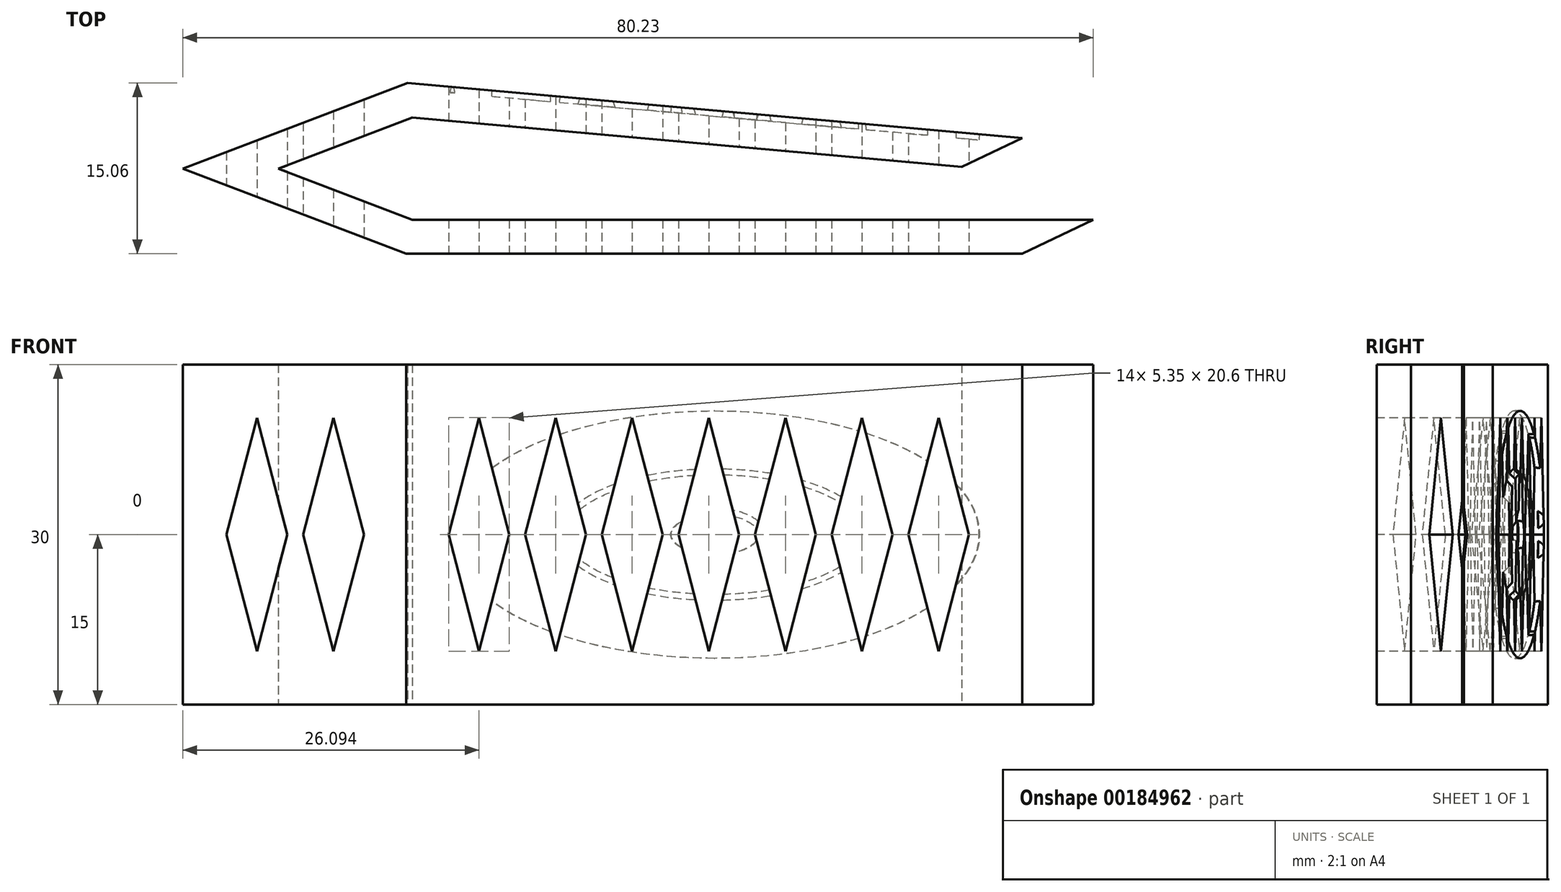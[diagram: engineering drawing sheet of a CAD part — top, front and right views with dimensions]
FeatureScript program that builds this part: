
annotation { "Feature Type Name" : "Feature", "Feature Type Description" : "" }
export const myFeature = defineFeature(function(context is Context, id is Id, definition is map)
    precondition{}
    {
        {
            var Q0;
            Q0=qCreatedBy(makeId("Top.planeOp"),FACE);
            var sketch = newSketch(context, id + "F0", { "sketchPlane" : qUnion([Q0])});
            skLineSegment(sketch, "E0", {"start": v(30.5, 0) * mm, "end": v(-29.5, 0) * mm});
            skLineSegment(sketch, "E1", {"start": v(-29.5, 9) * mm, "end": v(18.93, 4.67) * mm});
            skLineSegment(sketch, "E2", {"start": v(18.93, 4.67) * mm, "end": v(24.23, 7.2) * mm});
            skLineSegment(sketch, "E3", {"start": v(24.23, -3) * mm, "end": v(30.5, 0) * mm});
            skLineSegment(sketch, "E4.0", {"start": v(-29.92, 12.06) * mm, "end": v(24.23, 7.2) * mm});
            skLineSegment(sketch, "E5.0", {"start": v(24.23, -3) * mm, "end": v(-30.05, -3) * mm});
            skLineSegment(sketch, "E6", {"start": v(-29.5, 9) * mm, "end": v(-29.5, 0) * mm, "construction": true});
            skLineSegment(sketch, "E7", {"start": v(-29.5, 4.5) * mm, "end": v(-112.6, 4.5) * mm, "construction": true});
            skLineSegment(sketch, "E8", {"start": v(-29.5, 9) * mm, "end": v(-41.3, 4.5) * mm});
            skLineSegment(sketch, "E9", {"start": v(-41.3, 4.5) * mm, "end": v(-29.5, 0) * mm});
            skLineSegment(sketch, "E10", {"start": v(-29.92, 12.06) * mm, "end": v(-49.73, 4.5) * mm});
            skLineSegment(sketch, "E11", {"start": v(-49.73, 4.5) * mm, "end": v(-30.05, -3) * mm});
            skPoint(sketch, "E12.orphan", {"position": v(30.5, -3) * mm});
            skLineSegment(sketch, "E13", {"start": v(-38.13, 8.93) * mm, "end": v(-37.06, 6.12) * mm, "construction": true});
            skLineSegment(sketch, "E14", {"start": v(-34.51, 1.91) * mm, "end": v(-35.58, -0.9) * mm, "construction": true});
            skLineSegment(sketch, "E15", {"start": v(-29.92, 12.06) * mm, "end": v(-30.05, -3) * mm, "construction": true});
            skLineSegment(sketch, "E16", {"start": v(18.93, 4.67) * mm, "end": v(18.93, 0) * mm, "construction": true});
            skSolve(sketch);
        }
        {
            var Q0;
            Q0=makeQuery(id+"F0.imprint","IMPRINT",FACE,{"disambiguationData":[TD([[makeQuery(id+"F0.imprint","IMPRINT",EDGE,{"derivedFrom":sQuery(id+"F0.wireOp",EDGE,"E0")}),1.0]])]});
            extrude(context, id + "F1", {"entities" : qUnion([Q0]), "endBound" : BoundingType.SYMMETRIC, "depth" : 30 * mm});
        }
        {
            var Q0;
            Q0=makeQuery(id+"F1.opExtrude","SWEPT_FACE",FACE,{"disambiguationData":[OSD([sQuery(id+"F0.wireOp",EDGE,"E4.0")])]});
            cPlane(context, id + "F2", {"entities" : qUnion([Q0]), "cplaneType" : CPlaneType.OFFSET, "offset" : 0 * mm, "width" : 150 * mm, "height" : 150 * mm});
        }
        {
            var Q0;
            Q0=qCreatedBy(id+"F2.planeOp",FACE);
            var sketch = newSketch(context, id + "F3", { "sketchPlane" : qUnion([Q0])});
            skPoint(sketch, "E17.middle", {"position": v(3.69, 0) * mm});
            skPoint(sketch, "E18.orphan", {"position": v(19.84, -6.45) * mm});
            skPoint(sketch, "E19.orphan", {"position": v(27.88, -12.16) * mm});
            skPoint(sketch, "E20.orphan", {"position": v(-20.5, 12.16) * mm});
            skPoint(sketch, "E21.orphan", {"position": v(-12.47, 6.45) * mm});
            skPoint(sketch, "E22.orphan", {"position": v(-3.06, 2.36) * mm});
            skPoint(sketch, "E23.orphan", {"position": v(10.44, -2.36) * mm});
            skPoint(sketch, "E24.start.orphan", {"position": v(3.69, -15.05) * mm});
            skPoint(sketch, "E25.orphan", {"position": v(3.69, 15) * mm});
            skLineSegment(sketch, "E26.trimOffspring", {"start": v(-3.06, 0) * mm, "end": v(-3.2, 0) * mm});
            skLineSegment(sketch, "E27.trimOffspring", {"start": v(10.73, 0) * mm, "end": v(10.44, 0) * mm});
            skPoint(sketch, "E28.start.orphan", {"position": v(30.85, 0) * mm});
            skPoint(sketch, "E29.trimOffspring.end.orphan", {"position": v(-23.48, 0) * mm});
            skPoint(sketch, "E30.orphan", {"position": v(-23.48, -15.05) * mm});
            skPoint(sketch, "E31.orphan", {"position": v(30.85, -15.05) * mm});
            skPoint(sketch, "E32.orphan", {"position": v(30.85, 15) * mm});
            skPoint(sketch, "E33.top.end.orphan", {"position": v(-23.48, 15) * mm});
            skEllipse(sketch, "E34", {"center": v(3.69, 0) * mm, "majorRadius": 23.4 * mm, "minorRadius": 10.9 * mm, "majorAxis": v(1, 0)});
            skEllipse(sketch, "E35", {"center": v(3.69, 0) * mm, "majorRadius": 13.72 * mm, "minorRadius": 5.78 * mm, "majorAxis": v(1, 0)});
            skEllipse(sketch, "E36", {"center": v(3.69, 0) * mm, "majorRadius": 3.87 * mm, "minorRadius": 1.8 * mm, "majorAxis": v(1, 0)});
            skSolve(sketch);
        }
        {
            var Q0;
            Q0=qCreatedBy(makeId("Front.planeOp"),FACE);
            var sketch = newSketch(context, id + "F4", { "sketchPlane" : qUnion([Q0])});
            skLineSegment(sketch, "E37", {"start": v(-29.93, 0) * mm, "end": v(-49.72, 0) * mm});
            skPoint(sketch, "E38.middle", {"position": v(-39.83, 0) * mm});
            skPoint(sketch, "E39.orphan", {"position": v(-33.77, 10.3) * mm});
            skPoint(sketch, "E40.orphan", {"position": v(-45.88, -10.3) * mm});
            skPoint(sketch, "E41.start.orphan", {"position": v(-39.83, 15.06) * mm});
            skPoint(sketch, "E42.orphan", {"position": v(-29.93, 15.06) * mm});
            skPoint(sketch, "E43.trimOffspring.end.orphan", {"position": v(-39.83, -14.93) * mm});
            skPoint(sketch, "E44.orphan", {"position": v(-29.93, -14.93) * mm});
            skPoint(sketch, "E45.orphan", {"position": v(-49.72, -14.93) * mm});
            skPoint(sketch, "E46.bottom.end.orphan", {"position": v(-49.72, 15.06) * mm});
            skPoint(sketch, "E47.orphan", {"position": v(-45.88, 10.3) * mm});
            skPoint(sketch, "E48.orphan", {"position": v(-33.77, -10.3) * mm});
            skLineSegment(sketch, "E49", {"start": v(-43.2, 10.3) * mm, "end": v(-45.88, 0) * mm});
            skLineSegment(sketch, "E50", {"start": v(-43.2, -10.3) * mm, "end": v(-45.88, 0) * mm});
            skLineSegment(sketch, "E51", {"start": v(-43.2, -10.3) * mm, "end": v(-40.53, 0) * mm});
            skLineSegment(sketch, "E52", {"start": v(-40.53, 0) * mm, "end": v(-43.2, 10.3) * mm});
            skLineSegment(sketch, "E53", {"start": v(-36.45, -10.3) * mm, "end": v(-33.77, 0) * mm});
            skLineSegment(sketch, "E54", {"start": v(-36.45, 10.3) * mm, "end": v(-39.13, 0) * mm});
            skLineSegment(sketch, "E55", {"start": v(-39.13, 0) * mm, "end": v(-36.45, -10.3) * mm});
            skLineSegment(sketch, "E56", {"start": v(-33.77, 0) * mm, "end": v(-36.45, 10.3) * mm});
            skLineSegment(sketch, "E57", {"start": v(-39.13, 0) * mm, "end": v(-33.77, 0) * mm, "construction": true});
            skLineSegment(sketch, "E58", {"start": v(-36.45, 10.3) * mm, "end": v(-36.45, -10.3) * mm, "construction": true});
            skLineSegment(sketch, "E59", {"start": v(-24.21, 10.3) * mm, "end": v(20.79, 10.3) * mm, "construction": true});
            skLineSegment(sketch, "E60", {"start": v(-24.21, -10.3) * mm, "end": v(16.14, -10.3) * mm, "construction": true});
            skLineSegment(sketch, "E61", {"start": v(0, 0) * mm, "end": v(-0.7, 0) * mm, "construction": true});
            skPoint(sketch, "E62", {"position": v(-0.7, 0) * mm});
            skLineSegment(sketch, "E63", {"start": v(-0.7, 0) * mm, "end": v(-6.05, 0) * mm, "construction": true});
            skLineSegment(sketch, "E64", {"start": v(-6.05, 0) * mm, "end": v(-7.45, 0) * mm, "construction": true});
            skLineSegment(sketch, "E65", {"start": v(-7.45, 0) * mm, "end": v(-12.8, 0) * mm, "construction": true});
            skLineSegment(sketch, "E66", {"start": v(-12.8, 0) * mm, "end": v(-14.2, 0) * mm, "construction": true});
            skLineSegment(sketch, "E67", {"start": v(-14.2, 0) * mm, "end": v(-19.56, 0) * mm, "construction": true});
            skLineSegment(sketch, "E68", {"start": v(-19.56, 0) * mm, "end": v(-20.96, 0) * mm, "construction": true});
            skLineSegment(sketch, "E69", {"start": v(-20.96, 0) * mm, "end": v(-26.31, 0) * mm, "construction": true});
            skLineSegment(sketch, "E70", {"start": v(0, 0) * mm, "end": v(0.7, 0) * mm, "construction": true});
            skLineSegment(sketch, "E71", {"start": v(0.7, 0) * mm, "end": v(6.05, 0) * mm, "construction": true});
            skLineSegment(sketch, "E72", {"start": v(6.05, 0) * mm, "end": v(7.45, 0) * mm, "construction": true});
            skLineSegment(sketch, "E73", {"start": v(7.45, 0) * mm, "end": v(12.8, 0) * mm, "construction": true});
            skLineSegment(sketch, "E74", {"start": v(12.8, 0) * mm, "end": v(14.2, 0) * mm, "construction": true});
            skLineSegment(sketch, "E75", {"start": v(14.2, 0) * mm, "end": v(19.56, 0) * mm, "construction": true});
            skLineSegment(sketch, "E76", {"start": v(-16.88, 0) * mm, "end": v(-16.88, 13.87) * mm, "construction": true});
            skLineSegment(sketch, "E77", {"start": v(-23.64, 0) * mm, "end": v(-23.64, 13.87) * mm, "construction": true});
            skLineSegment(sketch, "E78", {"start": v(-10.13, 0) * mm, "end": v(-10.13, 13.87) * mm, "construction": true});
            skLineSegment(sketch, "E79", {"start": v(-3.38, 0) * mm, "end": v(-3.38, 12.97) * mm, "construction": true});
            skLineSegment(sketch, "E80", {"start": v(3.38, 0) * mm, "end": v(3.38, 12.97) * mm, "construction": true});
            skLineSegment(sketch, "E81", {"start": v(10.13, 0) * mm, "end": v(10.13, 12.97) * mm, "construction": true});
            skLineSegment(sketch, "E82", {"start": v(16.88, 0) * mm, "end": v(16.88, 13.87) * mm, "construction": true});
            skLineSegment(sketch, "E83", {"start": v(-23.64, 0) * mm, "end": v(-23.64, -18.45) * mm, "construction": true});
            skLineSegment(sketch, "E84", {"start": v(-16.88, -17.49) * mm, "end": v(-16.88, 0) * mm, "construction": true});
            skLineSegment(sketch, "E85", {"start": v(-10.13, 0) * mm, "end": v(-10.13, -16.11) * mm, "construction": true});
            skLineSegment(sketch, "E86", {"start": v(-3.38, 0) * mm, "end": v(-3.38, -17.14) * mm, "construction": true});
            skLineSegment(sketch, "E87", {"start": v(3.38, -17.35) * mm, "end": v(3.38, 0) * mm, "construction": true});
            skLineSegment(sketch, "E88", {"start": v(10.13, 0) * mm, "end": v(10.13, -19.76) * mm, "construction": true});
            skLineSegment(sketch, "E89", {"start": v(16.88, -18.52) * mm, "end": v(16.88, 0) * mm, "construction": true});
            skLineSegment(sketch, "E90", {"start": v(-26.31, 0) * mm, "end": v(-23.64, 10.3) * mm});
            skLineSegment(sketch, "E91", {"start": v(-23.64, 10.3) * mm, "end": v(-20.96, 0) * mm});
            skLineSegment(sketch, "E92", {"start": v(-26.31, 0) * mm, "end": v(-23.64, -10.3) * mm});
            skLineSegment(sketch, "E93", {"start": v(-23.64, -10.3) * mm, "end": v(-20.96, 0) * mm});
            skLineSegment(sketch, "E94", {"start": v(-19.56, 0) * mm, "end": v(-16.88, 10.3) * mm});
            skLineSegment(sketch, "E95", {"start": v(-16.88, 10.3) * mm, "end": v(-14.2, 0) * mm});
            skLineSegment(sketch, "E96", {"start": v(-16.88, -10.3) * mm, "end": v(-14.2, 0) * mm});
            skLineSegment(sketch, "E97", {"start": v(-16.88, -10.3) * mm, "end": v(-19.56, 0) * mm});
            skLineSegment(sketch, "E98", {"start": v(-12.8, 0) * mm, "end": v(-10.13, 10.3) * mm});
            skLineSegment(sketch, "E99", {"start": v(-10.13, 10.3) * mm, "end": v(-7.45, 0) * mm});
            skLineSegment(sketch, "E100", {"start": v(-12.8, 0) * mm, "end": v(-10.13, -10.3) * mm});
            skLineSegment(sketch, "E101", {"start": v(-10.13, -10.3) * mm, "end": v(-7.45, 0) * mm});
            skLineSegment(sketch, "E102", {"start": v(-3.38, 10.3) * mm, "end": v(-6.05, 0) * mm});
            skLineSegment(sketch, "E103", {"start": v(-3.38, -10.3) * mm, "end": v(-0.7, 0) * mm});
            skLineSegment(sketch, "E104", {"start": v(-3.38, 10.3) * mm, "end": v(-0.7, 0) * mm});
            skLineSegment(sketch, "E105", {"start": v(-3.38, -10.3) * mm, "end": v(-6.05, 0) * mm});
            skLineSegment(sketch, "E106", {"start": v(3.38, 10.3) * mm, "end": v(0.7, 0) * mm});
            skLineSegment(sketch, "E107", {"start": v(3.38, -10.3) * mm, "end": v(6.05, 0) * mm});
            skLineSegment(sketch, "E108", {"start": v(3.38, 10.3) * mm, "end": v(6.05, 0) * mm});
            skLineSegment(sketch, "E109", {"start": v(0.7, 0) * mm, "end": v(3.38, -10.3) * mm});
            skLineSegment(sketch, "E110", {"start": v(10.13, -10.3) * mm, "end": v(12.8, 0) * mm});
            skLineSegment(sketch, "E111", {"start": v(10.13, 10.3) * mm, "end": v(12.8, 0) * mm});
            skLineSegment(sketch, "E112", {"start": v(14.2, 0) * mm, "end": v(16.88, 10.3) * mm});
            skLineSegment(sketch, "E113", {"start": v(16.88, 10.3) * mm, "end": v(19.56, 0) * mm});
            skLineSegment(sketch, "E114", {"start": v(16.88, -10.3) * mm, "end": v(14.2, 0) * mm});
            skLineSegment(sketch, "E115", {"start": v(19.56, 0) * mm, "end": v(16.88, -10.3) * mm});
            skLineSegment(sketch, "E116", {"start": v(10.13, -10.3) * mm, "end": v(7.45, 0) * mm});
            skLineSegment(sketch, "E117", {"start": v(10.13, 10.3) * mm, "end": v(7.45, 0) * mm});
            skSolve(sketch);
        }
        {
            var Q0;
            Q0 = qSketchRegion(id + "F4", true);
            extrude(context, id + "F5", {"entities" : qUnion([Q0]), "operationType" : NewBodyOperationType.REMOVE, "endBound" : BoundingType.SYMMETRIC, "oppositeDirection" : true, "depth" : 25 * mm});
        }
        {
            var Q0;
            Q0=makeQuery(id+"F3.imprint","IMPRINT",FACE,{"disambiguationData":[TD([[makeQuery(id+"F3.imprint","IMPRINT",EDGE,{"derivedFrom":sQuery(id+"F3.wireOp",EDGE,"E34")}),1.0]])]});
            extrude(context, id + "F6", {"entities" : qUnion([Q0]), "operationType" : NewBodyOperationType.REMOVE, "oppositeDirection" : true, "depth" : .5 * mm});
        }
        {
            var Q0;
            Q0=makeQuery(id+"F3.imprint","IMPRINT",FACE,{"disambiguationData":[TD([[makeQuery(id+"F3.imprint","IMPRINT",EDGE,{"derivedFrom":sQuery(id+"F3.wireOp",EDGE,"E36")}),1.0]])]});
            extrude(context, id + "F7", {"entities" : qUnion([Q0]), "operationType" : NewBodyOperationType.REMOVE, "oppositeDirection" : true, "depth" : .5 * mm});
        }
        {
            var Q0;
            {var subQ1=sQuery(id+"F3.wireOp",EDGE,"E34");var subQ2=makeQuery(id+"F1.opExtrude","SWEPT_FACE",FACE,{"disambiguationData":[OSD([sQuery(id+"F0.wireOp",EDGE,"E1")])]});Q0=makeQuery(id+"F6.boolean.opBoolean","COPY",EDGE,{"disambiguationData":[TD([makeQuery(id+"F5.boolean.opBoolean","COPY",FACE,{"disambiguationData":[TD([subQ2])],"derivedFrom":makeQuery(id+"F5.opExtrude","SWEPT_FACE",FACE,{"disambiguationData":[OSD([sQuery(id+"F4.wireOp",EDGE,"E95")])]})})])],"derivedFrom":makeQuery(id+"F6.opExtrude","CAP_EDGE",EDGE,{"disambiguationData":[OSD([subQ1])],"isStart":true})});}
            var Q1;
            {var subQ1=sQuery(id+"F3.wireOp",EDGE,"E34");var subQ2=makeQuery(id+"F1.opExtrude","SWEPT_FACE",FACE,{"disambiguationData":[OSD([sQuery(id+"F0.wireOp",EDGE,"E1")])]});Q1=makeQuery(id+"F6.boolean.opBoolean","COPY",EDGE,{"disambiguationData":[TD([makeQuery(id+"F5.boolean.opBoolean","COPY",FACE,{"disambiguationData":[TD([subQ2])],"derivedFrom":makeQuery(id+"F5.opExtrude","SWEPT_FACE",FACE,{"disambiguationData":[OSD([sQuery(id+"F4.wireOp",EDGE,"E111")])]})})])],"derivedFrom":makeQuery(id+"F6.opExtrude","CAP_EDGE",EDGE,{"disambiguationData":[OSD([subQ1])],"isStart":true})});}
            var Q2;
            {var subQ1=sQuery(id+"F3.wireOp",EDGE,"E34");var subQ3=makeQuery(id+"F1.opExtrude","SWEPT_FACE",FACE,{"disambiguationData":[OSD([sQuery(id+"F0.wireOp",EDGE,"E1")])]});var subQ5=makeQuery(id+"F5.opExtrude","SWEPT_FACE",FACE,{"disambiguationData":[OSD([sQuery(id+"F4.wireOp",EDGE,"E113")])]});Q2=makeQuery(id+"F6.boolean.opBoolean","COPY",EDGE,{"disambiguationData":[TD([makeQuery(id+"F5.boolean.opBoolean","COPY",FACE,{"disambiguationData":[TD([subQ3])],"derivedFrom":subQ5})])],"derivedFrom":makeQuery(id+"F6.opExtrude","CAP_EDGE",EDGE,{"disambiguationData":[OSD([subQ1])],"isStart":true})});}
            var Q3;
            {var subQ1=sQuery(id+"F3.wireOp",EDGE,"E34");var subQ2=makeQuery(id+"F1.opExtrude","SWEPT_FACE",FACE,{"disambiguationData":[OSD([sQuery(id+"F0.wireOp",EDGE,"E1")])]});Q3=makeQuery(id+"F6.boolean.opBoolean","COPY",EDGE,{"disambiguationData":[TD([makeQuery(id+"F5.boolean.opBoolean","COPY",FACE,{"disambiguationData":[TD([subQ2])],"derivedFrom":makeQuery(id+"F5.opExtrude","SWEPT_FACE",FACE,{"disambiguationData":[OSD([sQuery(id+"F4.wireOp",EDGE,"E110")])]})})])],"derivedFrom":makeQuery(id+"F6.opExtrude","CAP_EDGE",EDGE,{"disambiguationData":[OSD([subQ1])],"isStart":true})});}
            var Q4;
            {var subQ1=sQuery(id+"F3.wireOp",EDGE,"E34");var subQ2=makeQuery(id+"F1.opExtrude","SWEPT_FACE",FACE,{"disambiguationData":[OSD([sQuery(id+"F0.wireOp",EDGE,"E1")])]});Q4=makeQuery(id+"F6.boolean.opBoolean","COPY",EDGE,{"disambiguationData":[TD([makeQuery(id+"F5.boolean.opBoolean","COPY",FACE,{"disambiguationData":[TD([subQ2])],"derivedFrom":makeQuery(id+"F5.opExtrude","SWEPT_FACE",FACE,{"disambiguationData":[OSD([sQuery(id+"F4.wireOp",EDGE,"E96")])]})})])],"derivedFrom":makeQuery(id+"F6.opExtrude","CAP_EDGE",EDGE,{"disambiguationData":[OSD([subQ1])],"isStart":true})});}
            var Q5;
            {var subQ1=sQuery(id+"F3.wireOp",EDGE,"E34");var subQ2=makeQuery(id+"F1.opExtrude","SWEPT_FACE",FACE,{"disambiguationData":[OSD([sQuery(id+"F0.wireOp",EDGE,"E1")])]});Q5=makeQuery(id+"F6.boolean.opBoolean","COPY",EDGE,{"disambiguationData":[TD([makeQuery(id+"F5.boolean.opBoolean","COPY",FACE,{"disambiguationData":[TD([subQ2])],"derivedFrom":makeQuery(id+"F5.opExtrude","SWEPT_FACE",FACE,{"disambiguationData":[OSD([sQuery(id+"F4.wireOp",EDGE,"E91")])]})})])],"derivedFrom":makeQuery(id+"F6.opExtrude","CAP_EDGE",EDGE,{"disambiguationData":[OSD([subQ1])],"isStart":true})});}
            var Q6;
            {var subQ1=sQuery(id+"F3.wireOp",EDGE,"E34");var subQ2=makeQuery(id+"F1.opExtrude","SWEPT_FACE",FACE,{"disambiguationData":[OSD([sQuery(id+"F0.wireOp",EDGE,"E1")])]});Q6=makeQuery(id+"F6.boolean.opBoolean","COPY",EDGE,{"disambiguationData":[TD([makeQuery(id+"F5.boolean.opBoolean","COPY",FACE,{"disambiguationData":[TD([subQ2])],"derivedFrom":makeQuery(id+"F5.opExtrude","SWEPT_FACE",FACE,{"disambiguationData":[OSD([sQuery(id+"F4.wireOp",EDGE,"E93")])]})})])],"derivedFrom":makeQuery(id+"F6.opExtrude","CAP_EDGE",EDGE,{"disambiguationData":[OSD([subQ1])],"isStart":true})});}
            var Q7;
            {var subQ1=makeQuery(id+"F1.opExtrude","SWEPT_FACE",FACE,{"disambiguationData":[OSD([sQuery(id+"F0.wireOp",EDGE,"E1")])]});var subQ2=sQuery(id+"F3.wireOp",EDGE,"E36");Q7=makeQuery(id+"F7.boolean.opBoolean","COPY",EDGE,{"disambiguationData":[TD([makeQuery(id+"F5.boolean.opBoolean","COPY",FACE,{"disambiguationData":[TD([subQ1])],"derivedFrom":makeQuery(id+"F5.opExtrude","SWEPT_FACE",FACE,{"disambiguationData":[OSD([sQuery(id+"F4.wireOp",EDGE,"E104")])]})})])],"derivedFrom":makeQuery(id+"F7.opExtrude","CAP_EDGE",EDGE,{"disambiguationData":[OSD([subQ2])],"isStart":true})});}
            var Q8;
            {var subQ1=makeQuery(id+"F1.opExtrude","SWEPT_FACE",FACE,{"disambiguationData":[OSD([sQuery(id+"F0.wireOp",EDGE,"E1")])]});var subQ3=makeQuery(id+"F5.opExtrude","SWEPT_FACE",FACE,{"disambiguationData":[OSD([sQuery(id+"F4.wireOp",EDGE,"E102")])]});var subQ4=sQuery(id+"F3.wireOp",EDGE,"E36");Q8=makeQuery(id+"F7.boolean.opBoolean","COPY",EDGE,{"disambiguationData":[TD([makeQuery(id+"F5.boolean.opBoolean","COPY",FACE,{"disambiguationData":[TD([subQ1])],"derivedFrom":subQ3})])],"derivedFrom":makeQuery(id+"F7.opExtrude","CAP_EDGE",EDGE,{"disambiguationData":[OSD([subQ4])],"isStart":true})});}
            var Q9;
            {var subQ1=makeQuery(id+"F1.opExtrude","SWEPT_FACE",FACE,{"disambiguationData":[OSD([sQuery(id+"F0.wireOp",EDGE,"E1")])]});var subQ2=sQuery(id+"F3.wireOp",EDGE,"E36");Q9=makeQuery(id+"F7.boolean.opBoolean","COPY",EDGE,{"disambiguationData":[TD([makeQuery(id+"F5.boolean.opBoolean","COPY",FACE,{"disambiguationData":[TD([subQ1])],"derivedFrom":makeQuery(id+"F5.opExtrude","SWEPT_FACE",FACE,{"disambiguationData":[OSD([sQuery(id+"F4.wireOp",EDGE,"E103")])]})})])],"derivedFrom":makeQuery(id+"F7.opExtrude","CAP_EDGE",EDGE,{"disambiguationData":[OSD([subQ2])],"isStart":true})});}
            var Q10;
            {var subQ1=makeQuery(id+"F1.opExtrude","SWEPT_FACE",FACE,{"disambiguationData":[OSD([sQuery(id+"F0.wireOp",EDGE,"E1")])]});var subQ2=sQuery(id+"F3.wireOp",EDGE,"E35");Q10=makeQuery(id+"F6.boolean.opBoolean","COPY",EDGE,{"disambiguationData":[TD([makeQuery(id+"F5.boolean.opBoolean","COPY",FACE,{"disambiguationData":[TD([subQ1])],"derivedFrom":makeQuery(id+"F5.opExtrude","SWEPT_FACE",FACE,{"disambiguationData":[OSD([sQuery(id+"F4.wireOp",EDGE,"E107")])]})})])],"derivedFrom":makeQuery(id+"F6.opExtrude","CAP_EDGE",EDGE,{"disambiguationData":[OSD([subQ2])],"isStart":true})});}
            var Q11;
            {var subQ1=makeQuery(id+"F1.opExtrude","SWEPT_FACE",FACE,{"disambiguationData":[OSD([sQuery(id+"F0.wireOp",EDGE,"E1")])]});var subQ2=sQuery(id+"F3.wireOp",EDGE,"E35");Q11=makeQuery(id+"F6.boolean.opBoolean","COPY",EDGE,{"disambiguationData":[TD([makeQuery(id+"F5.boolean.opBoolean","COPY",FACE,{"disambiguationData":[TD([subQ1])],"derivedFrom":makeQuery(id+"F5.opExtrude","SWEPT_FACE",FACE,{"disambiguationData":[OSD([sQuery(id+"F4.wireOp",EDGE,"E103")])]})})])],"derivedFrom":makeQuery(id+"F6.opExtrude","CAP_EDGE",EDGE,{"disambiguationData":[OSD([subQ2])],"isStart":true})});}
            var Q12;
            {var subQ1=makeQuery(id+"F1.opExtrude","SWEPT_FACE",FACE,{"disambiguationData":[OSD([sQuery(id+"F0.wireOp",EDGE,"E1")])]});var subQ2=sQuery(id+"F3.wireOp",EDGE,"E35");Q12=makeQuery(id+"F6.boolean.opBoolean","COPY",EDGE,{"disambiguationData":[TD([makeQuery(id+"F5.boolean.opBoolean","COPY",FACE,{"disambiguationData":[TD([subQ1])],"derivedFrom":makeQuery(id+"F5.opExtrude","SWEPT_FACE",FACE,{"disambiguationData":[OSD([sQuery(id+"F4.wireOp",EDGE,"E101")])]})})])],"derivedFrom":makeQuery(id+"F6.opExtrude","CAP_EDGE",EDGE,{"disambiguationData":[OSD([subQ2])],"isStart":true})});}
            var Q13;
            {var subQ1=makeQuery(id+"F1.opExtrude","SWEPT_FACE",FACE,{"disambiguationData":[OSD([sQuery(id+"F0.wireOp",EDGE,"E1")])]});var subQ2=sQuery(id+"F3.wireOp",EDGE,"E35");Q13=makeQuery(id+"F6.boolean.opBoolean","COPY",EDGE,{"disambiguationData":[TD([makeQuery(id+"F5.boolean.opBoolean","COPY",FACE,{"disambiguationData":[TD([subQ1])],"derivedFrom":makeQuery(id+"F5.opExtrude","SWEPT_FACE",FACE,{"disambiguationData":[OSD([sQuery(id+"F4.wireOp",EDGE,"E96")])]})})])],"derivedFrom":makeQuery(id+"F6.opExtrude","CAP_EDGE",EDGE,{"disambiguationData":[OSD([subQ2])],"isStart":true})});}
            var Q14;
            {var subQ1=makeQuery(id+"F1.opExtrude","SWEPT_FACE",FACE,{"disambiguationData":[OSD([sQuery(id+"F0.wireOp",EDGE,"E1")])]});var subQ2=sQuery(id+"F3.wireOp",EDGE,"E35");Q14=makeQuery(id+"F6.boolean.opBoolean","COPY",EDGE,{"disambiguationData":[TD([makeQuery(id+"F5.boolean.opBoolean","COPY",FACE,{"disambiguationData":[TD([subQ1])],"derivedFrom":makeQuery(id+"F5.opExtrude","SWEPT_FACE",FACE,{"disambiguationData":[OSD([sQuery(id+"F4.wireOp",EDGE,"E95")])]})})])],"derivedFrom":makeQuery(id+"F6.opExtrude","CAP_EDGE",EDGE,{"disambiguationData":[OSD([subQ2])],"isStart":true})});}
            var Q15;
            {var subQ1=makeQuery(id+"F1.opExtrude","SWEPT_FACE",FACE,{"disambiguationData":[OSD([sQuery(id+"F0.wireOp",EDGE,"E1")])]});var subQ2=sQuery(id+"F3.wireOp",EDGE,"E35");Q15=makeQuery(id+"F6.boolean.opBoolean","COPY",EDGE,{"disambiguationData":[TD([makeQuery(id+"F5.boolean.opBoolean","COPY",FACE,{"disambiguationData":[TD([subQ1])],"derivedFrom":makeQuery(id+"F5.opExtrude","SWEPT_FACE",FACE,{"disambiguationData":[OSD([sQuery(id+"F4.wireOp",EDGE,"E99")])]})})])],"derivedFrom":makeQuery(id+"F6.opExtrude","CAP_EDGE",EDGE,{"disambiguationData":[OSD([subQ2])],"isStart":true})});}
            var Q16;
            {var subQ1=makeQuery(id+"F1.opExtrude","SWEPT_FACE",FACE,{"disambiguationData":[OSD([sQuery(id+"F0.wireOp",EDGE,"E1")])]});var subQ2=sQuery(id+"F3.wireOp",EDGE,"E35");Q16=makeQuery(id+"F6.boolean.opBoolean","COPY",EDGE,{"disambiguationData":[TD([makeQuery(id+"F5.boolean.opBoolean","COPY",FACE,{"disambiguationData":[TD([subQ1])],"derivedFrom":makeQuery(id+"F5.opExtrude","SWEPT_FACE",FACE,{"disambiguationData":[OSD([sQuery(id+"F4.wireOp",EDGE,"E104")])]})})])],"derivedFrom":makeQuery(id+"F6.opExtrude","CAP_EDGE",EDGE,{"disambiguationData":[OSD([subQ2])],"isStart":true})});}
            var Q17;
            {var subQ1=makeQuery(id+"F1.opExtrude","SWEPT_FACE",FACE,{"disambiguationData":[OSD([sQuery(id+"F0.wireOp",EDGE,"E1")])]});var subQ2=sQuery(id+"F3.wireOp",EDGE,"E35");Q17=makeQuery(id+"F6.boolean.opBoolean","COPY",EDGE,{"disambiguationData":[TD([makeQuery(id+"F5.boolean.opBoolean","COPY",FACE,{"disambiguationData":[TD([subQ1])],"derivedFrom":makeQuery(id+"F5.opExtrude","SWEPT_FACE",FACE,{"disambiguationData":[OSD([sQuery(id+"F4.wireOp",EDGE,"E108")])]})})])],"derivedFrom":makeQuery(id+"F6.opExtrude","CAP_EDGE",EDGE,{"disambiguationData":[OSD([subQ2])],"isStart":true})});}
            chamfer(context, id + "F8", {"entities" : qUnion([Q0, Q1, Q2, Q3, Q4, Q5, Q6, Q7, Q8, Q9, Q10, Q11, Q12, Q13, Q14, Q15, Q16, Q17]), "width" : .5 * mm, "tangentPropagation" : true});
        }
    });
